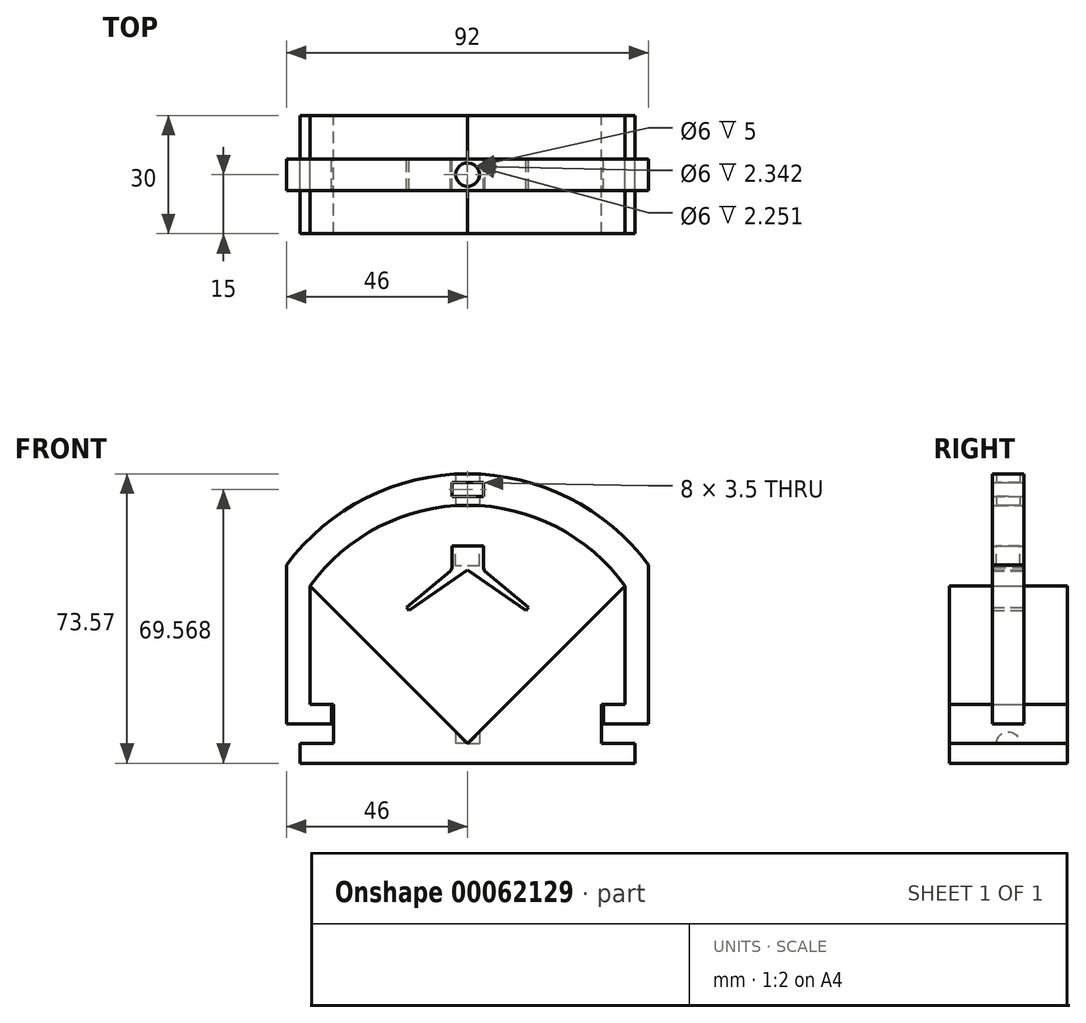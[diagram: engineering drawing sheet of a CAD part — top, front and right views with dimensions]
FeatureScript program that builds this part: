
annotation { "Feature Type Name" : "Feature", "Feature Type Description" : "" }
export const myFeature = defineFeature(function(context is Context, id is Id, definition is map)
    precondition{}
    {
        {
            var Q0;
            Q0=qCreatedBy(makeId("Top.planeOp"),FACE);
            var sketch = newSketch(context, id + "F0", { "sketchPlane" : qUnion([Q0])});
            skLineSegment(sketch, "E0.rect.bottom", {"start": v(42.5, -15) * mm, "end": v(-42.5, -15) * mm});
            skLineSegment(sketch, "E0.rect.top", {"start": v(42.5, 15) * mm, "end": v(-42.5, 15) * mm});
            skLineSegment(sketch, "E0.rect.left", {"start": v(42.5, -15) * mm, "end": v(42.5, 15) * mm});
            skLineSegment(sketch, "E0.rect.right", {"start": v(-42.5, -15) * mm, "end": v(-42.5, 15) * mm});
            skPoint(sketch, "E0.rect.middle", {"position": v(0, 0) * mm});
            skSolve(sketch);
        }
        {
            var Q0;
            Q0 = qSketchRegion(id + "F0", true);
            extrude(context, id + "F1", {"entities" : qUnion([Q0]), "oppositeDirection" : true, "depth" : 5 * mm});
        }
        {
            var Q0;
            Q0=qCreatedBy(makeId("Front.planeOp"),FACE);
            var sketch = newSketch(context, id + "F2", { "sketchPlane" : qUnion([Q0])});
            skLineSegment(sketch, "E1", {"start": v(0, 0) * mm, "end": v(-40, 40) * mm});
            skLineSegment(sketch, "E2", {"start": v(-34, 0) * mm, "end": v(0, 0) * mm});
            skLineSegment(sketch, "E3", {"start": v(-40, 40) * mm, "end": v(-40, 10) * mm});
            skLineSegment(sketch, "E4", {"start": v(-40, 10) * mm, "end": v(-34, 10) * mm});
            skLineSegment(sketch, "E5", {"start": v(-34, 10) * mm, "end": v(-34, 0) * mm});
            skLineSegment(sketch, "E6.MirrorCS", {"start": v(34, 0) * mm, "end": v(0, 0) * mm});
            skLineSegment(sketch, "E7.MirrorCS", {"start": v(34, 10) * mm, "end": v(34, 0) * mm});
            skLineSegment(sketch, "E8.MirrorCS", {"start": v(40, 10) * mm, "end": v(34, 10) * mm});
            skLineSegment(sketch, "E9.MirrorCS", {"start": v(0, 0) * mm, "end": v(40, 40) * mm});
            skLineSegment(sketch, "E10.MirrorCS", {"start": v(40, 40) * mm, "end": v(40, 10) * mm});
            skSolve(sketch);
        }
        {
            var Q0;
            Q0=makeQuery(id+"F2.imprint","IMPRINT",FACE,{"disambiguationData":[TD([[makeQuery(id+"F2.imprint","IMPRINT",EDGE,{"derivedFrom":sQuery(id+"F2.wireOp",EDGE,"E1")}),1.0]])]});
            var Q1;
            Q1=makeQuery(id+"F2.imprint","IMPRINT",FACE,{"disambiguationData":[TD([[makeQuery(id+"F2.imprint","IMPRINT",EDGE,{"derivedFrom":sQuery(id+"F2.wireOp",EDGE,"E6.MirrorCS")}),-1.0]])]});
            extrude(context, id + "F3", {"entities" : qUnion([Q0, Q1]), "operationType" : NewBodyOperationType.ADD, "depth" : 30 * mm, "symmetric" : true});
        }
        {
            var Q0;
            Q0=qCreatedBy(makeId("Front.planeOp"),FACE);
            var sketch = newSketch(context, id + "F4", { "sketchPlane" : qUnion([Q0])});
            skLineSegment(sketch, "E11.0", {"start": v(-40, 40) * mm, "end": v(-40, 10) * mm});
            skLineSegment(sketch, "E12.0", {"start": v(-40, 10) * mm, "end": v(-34.5, 10) * mm});
            skLineSegment(sketch, "E13", {"start": v(-34.5, 10) * mm, "end": v(-34.5, 5) * mm});
            skLineSegment(sketch, "E14", {"start": v(-34.5, 5) * mm, "end": v(-46, 5) * mm});
            skLineSegment(sketch, "E15", {"start": v(-46, 5) * mm, "end": v(-46, 45.35) * mm});
            skArc(sketch, "E16", {"start": v(0, 60.57) * mm, "mid": v(-22.49, 55.12) * mm, "end": v(-40, 40) * mm});
            skArc(sketch, "E17", {"start": v(0, 68.57) * mm, "mid": v(-25.76, 62.44) * mm, "end": v(-46, 45.35) * mm});
            skArc(sketch, "E18.MirrorCS", {"start": v(0, 60.57) * mm, "mid": v(22.49, 55.12) * mm, "end": v(40, 40) * mm});
            skArc(sketch, "E19.MirrorCS", {"start": v(0, 68.57) * mm, "mid": v(25.76, 62.44) * mm, "end": v(46, 45.35) * mm});
            skLineSegment(sketch, "E20.MirrorCS", {"start": v(46, 5) * mm, "end": v(46, 45.35) * mm});
            skLineSegment(sketch, "E21.MirrorCS", {"start": v(34.5, 5) * mm, "end": v(46, 5) * mm});
            skLineSegment(sketch, "E22.MirrorCS", {"start": v(34.5, 10) * mm, "end": v(34.5, 5) * mm});
            skLineSegment(sketch, "E23.MirrorCS", {"start": v(40, 40) * mm, "end": v(40, 10) * mm});
            skLineSegment(sketch, "E24.MirrorCS", {"start": v(40, 10) * mm, "end": v(34.5, 10) * mm});
            skLineSegment(sketch, "E25", {"start": v(0, 68.57) * mm, "end": v(0, 60.57) * mm, "construction": true});
            skPoint(sketch, "E26", {"position": v(0, 64.57) * mm});
            skLineSegment(sketch, "E27.bottom", {"start": v(0, 66.32) * mm, "end": v(-4, 66.32) * mm});
            skLineSegment(sketch, "E27.top", {"start": v(0, 62.82) * mm, "end": v(-4, 62.82) * mm});
            skLineSegment(sketch, "E27.left", {"start": v(0, 66.32) * mm, "end": v(0, 62.82) * mm, "construction": true});
            skLineSegment(sketch, "E27.right", {"start": v(-4, 66.32) * mm, "end": v(-4, 62.82) * mm});
            skLineSegment(sketch, "E28.MirrorCS", {"start": v(0, 62.82) * mm, "end": v(4, 62.82) * mm});
            skLineSegment(sketch, "E29.MirrorCS", {"start": v(0, 66.32) * mm, "end": v(4, 66.32) * mm});
            skLineSegment(sketch, "E30.MirrorCS", {"start": v(4, 66.32) * mm, "end": v(4, 62.82) * mm});
            skSolve(sketch);
        }
        {
            var Q0;
            Q0=makeQuery(id+"F4.imprint","IMPRINT",FACE,{"disambiguationData":[TD([[makeQuery(id+"F4.imprint","IMPRINT",EDGE,{"derivedFrom":sQuery(id+"F4.wireOp",EDGE,"E11.0")}),-1.0]])]});
            extrude(context, id + "F5", {"entities" : qUnion([Q0]), "depth" : 8 * mm, "symmetric" : true});
        }
        {
            var Q0;
            Q0=qCreatedBy(makeId("Top.planeOp"),FACE);
            var sketch = newSketch(context, id + "F6", { "sketchPlane" : qUnion([Q0])});
            skCircle(sketch, "E31", {"center": v(0, 0) * mm, "radius": 3 * mm});
            skSolve(sketch);
        }
        {
            var Q0;
            Q0 = qSketchRegion(id + "F6", true);
            extrude(context, id + "F7", {"entities" : qUnion([Q0]), "operationType" : NewBodyOperationType.REMOVE, "depth" : 80 * mm});
        }
        {
            var Q0;
            Q0=qCreatedBy(makeId("Front.planeOp"),FACE);
            var sketch = newSketch(context, id + "F8", { "sketchPlane" : qUnion([Q0])});
            skLineSegment(sketch, "E32", {"start": v(0, 50.18) * mm, "end": v(-4, 50.18) * mm});
            skLineSegment(sketch, "E33", {"start": v(-4, 50.18) * mm, "end": v(-4, 44.18) * mm});
            skLineSegment(sketch, "E34", {"start": v(-4, 44.18) * mm, "end": v(-15.5, 34.55) * mm});
            skLineSegment(sketch, "E35", {"start": v(-15.5, 34.55) * mm, "end": v(-14.85, 33.78) * mm});
            skLineSegment(sketch, "E36", {"start": v(-14.85, 33.78) * mm, "end": v(0, 44.18) * mm});
            skLineSegment(sketch, "E37.MirrorCS", {"start": v(0, 50.18) * mm, "end": v(4, 50.18) * mm});
            skLineSegment(sketch, "E38.MirrorCS", {"start": v(4, 50.18) * mm, "end": v(4, 44.18) * mm});
            skLineSegment(sketch, "E39.MirrorCS", {"start": v(4, 44.18) * mm, "end": v(15.5, 34.55) * mm});
            skLineSegment(sketch, "E40.MirrorCS", {"start": v(14.85, 33.78) * mm, "end": v(0, 44.18) * mm});
            skLineSegment(sketch, "E41.MirrorCS", {"start": v(15.5, 34.55) * mm, "end": v(14.85, 33.78) * mm});
            skSolve(sketch);
        }
        {
            var Q0;
            Q0=makeQuery(id+"F8.imprint","IMPRINT",FACE,{"disambiguationData":[TD([[makeQuery(id+"F8.imprint","IMPRINT",EDGE,{"derivedFrom":sQuery(id+"F8.wireOp",EDGE,"E32")}),1.0]])]});
            extrude(context, id + "F9", {"entities" : qUnion([Q0]), "depth" : 8 * mm, "symmetric" : true});
        }
        {
            var Q0;
            Q0=makeQuery(id+"F9.opExtrude","SWEPT_FACE",FACE,{"disambiguationData":[OSD([sQuery(id+"F8.wireOp",EDGE,"E32"),sQuery(id+"F8.wireOp",EDGE,"E37.MirrorCS")])]});
            var sketch = newSketch(context, id + "F10", { "sketchPlane" : qUnion([Q0])});
            skCircle(sketch, "E42", {"center": v(0, 0) * mm, "radius": 3 * mm});
            skSolve(sketch);
        }
        {
            var Q0;
            Q0 = qSketchRegion(id + "F10", true);
            extrude(context, id + "F11", {"entities" : qUnion([Q0]), "operationType" : NewBodyOperationType.REMOVE, "oppositeDirection" : true, "depth" : 5 * mm});
        }
        {
            var Q0;
            Q0=makeQuery(id+"F9.opExtrude","SWEPT_EDGE",EDGE,{"disambiguationData":[OSD([sQuery(id+"F8.wireOp",EDGE,"E33"),sQuery(id+"F8.wireOp",EDGE,"E34")])]});
            var Q1;
            Q1=makeQuery(id+"F9.opExtrude","SWEPT_EDGE",EDGE,{"disambiguationData":[OSD([sQuery(id+"F8.wireOp",EDGE,"E38.MirrorCS"),sQuery(id+"F8.wireOp",EDGE,"E39.MirrorCS")])]});
            chamfer(context, id + "F12", {"entities" : qUnion([Q0, Q1]), "width" : 1 * mm, "tangentPropagation" : true});
        }
    });
